# Revit family: B 0375 SLS
name_source: partatom
category: Lighting Fixtures
revit_build: Autodesk Revit 2017 (Build: 20160225_1515(x64)
units: mm (PartAtom-declared; Revit-internal decimal feet)

## family parameters
Cut with Voids When Loaded = No
Host = Face
Light Source = Yes
Part Type = Normal
Room Calculation Point = No
Round Connector Dimension = Use Diameter
Shared = No

## types (26) — shared parameters
Color Filter = 16777215
Default Elevation = 1219 mm
Dimming Lamp Color Temperature Shift = <None>
Emit Shape Visible in Rendering = Yes
Emit from Rectangle Length = 205 mm  [stored 0.672572 ft]
Emit from Rectangle Width = 229 mm
Lamp = LED
Manufacturer = ARLIGHT AYDINLATMA
Model = B0375SLS
Tilt Angle = 90.00°
Type Comments = Floodlight
URL = www.arlight.net/en/products/outdoor-lighting-fixture/solis/b-0375-sls

## per-type parameters (varying)
| type | Apparent Load | Description | Photometric Web File | Wattage Comments |
| BSLS.0375.140.40.15 | 140 VA | Beam Angle : 15° | b-0375-sls-140w-4k-70ra-e2sb-15d-09.ies | 140W |
| BSLS.0375.140.25 | 140 VA | Beam Angle : 25° | b-0375-sls-140w-4k-70ra-e2sb-25d-09.ies | 140W |
| BSLS.0375.140.40.70 | 140 VA | Beam Angle : 70° | b-0375-sls-140w-4k-70ra-e2sb-70d-09.ies | 140W |
| BSLS.0375.140.40.100 | 140 VA | Beam Angle : 100° | b-0375-sls-140w-4k-70ra-e2sb-100d-09.ies | 140W |
| BSLS.0375.140.40.20115 | 140 VA | Beam Angle : 20°+115° | b-0375-sls-140w-4k-70ra-e2sb-20d-115d-09.ies | 140W |
| BSLS.0375.140.40.ASL8 | 140 VA | Beam Angle : ASM-L8 | b-0375-sls-140w-4k-70ra-e2sb-asym-l8-09.ies | 140W |
| BSLS.0375.105.40.15 | 100 VA | Beam Angle : 15° | b-0375-sls-105w-4k-70ra-e2sb-15d-07.ies | 105W |
| BSLS.0375.105.40.25 | 100 VA | Beam Angle : 25° | b-0375-sls-105w-4k-70ra-e2sb-25d-07.ies | 105W |
| BSLS.0375.105.40.70 | 100 VA | Beam Angle : 70° | b-0375-sls-105w-4k-70ra-e2sb-70d-07.ies | 105W |
| BSLS.0375.105.40.100 | 100 VA | Beam Angle : 100° | b-0375-sls-105w-4k-70ra-e2sb-100d-07.ies | 105W |
| BSLS.0375.105.40.20115 | 100 VA | Beam Angle : 20°+115° | b-0375-sls-105w-4k-70ra-e2sb-20d-115d-07.ies | 105W |
| BSLS.0375.105.40.ASL8 | 100 VA | Beam Angle : ASM-L8 | b-0375-sls-105w-4k-70ra-e2sb-asm-l8-07.ies | 105W |
| BSLS.0375.69.40.ASL8 | 69 VA | Beam Angle : ASM-L8 | b-0375-sls-69w-4k-70ra-e2sb-asm-l8-05.ies | 69W |
| BSLS.0375.69.40.15 | 69 VA | Beam Angle : 15 | b-0375-sls-69w-4k-70ra-e2sb-15d-05.ies | 69W |
| BSLS.0375.69.40.25 | 69 VA | Beam Angle : 25 | b-0375-sls-69w-4k-70ra-e2sb-25d-05.ies | 69W |
| BSLS.0375.69.40.70 | 69 VA | Beam Angle : 70 | b-0375-sls-69w-4k-70ra-e2sb-70d-05.ies | 69W |
| BSLS.0375.69.40.100 | 69 VA | Beam Angle : 100 | b-0375-sls-69w-4k-70ra-e2sb-100d-05.ies | 69W |
| BSLS.0375.69.40.20115 | 69 VA | Beam Angle : 135 | b-0375-sls-69w-4k-70rai-e2sb-20d-115d-05.ies | 69W |
| BSLS.0375.69.40.ASL4 | 69 VA | Beam Angle : ASM-L4 | b-0375-sls-69w-4k-70ra-e2sb-asym-l4-05.ies | 69W |
| BSLS.0375.48.40.15 | 48 VA | Beam Angle : 15 | b-0375-sls-48w-4k-70ra-e2sb-15drc-035.ies | 69W |
| BSLS.0375.48.40.25 | 48 VA | Beam Angle : 25 | b-0375-sls-48w-4k-70ra-e2sb-25d-035.ies | 69W |
| BSLS.0375.48.40.70 | 48 VA | Beam Angle : 70 | b-0375-sls-48w-4k-70ra-e2sb-70drc-035.ies | 69W |
| BSLS.0375.48.40.100 | 48 VA | Beam Angle : 100 | b-0375-sls-48w-4k-70ra-e2sb-100drc-035.ies | 69W |
| BSLS.0375.48.40.20115 | 48 VA | Beam Angle : 135 | b-0375-sls-48w-4k-70ra-e2sb-20d-115d-035.ies | 69W |
| BSLS.0375.48.40.ASL4 | 48 VA | Beam Angle : ASM-L4 | b-0375-sls-48w-4k-70ra-e2sb-asm-l4-035.ies | 69W |
| BSLS.0375.48.40.ASL8 | 48 VA | Beam Angle : ASM-L8 | b-0375-sls-48w-4k-70ra-e2sb-asm-l8-035.ies | 69W |

note: [stored X ft] marks values corroborated as IEEE doubles in the binary element streams (Revit-internal decimal feet)

## geometry (parser evidence)
native form markers: Sweep x2
no freeform markers — native parametric forms only
